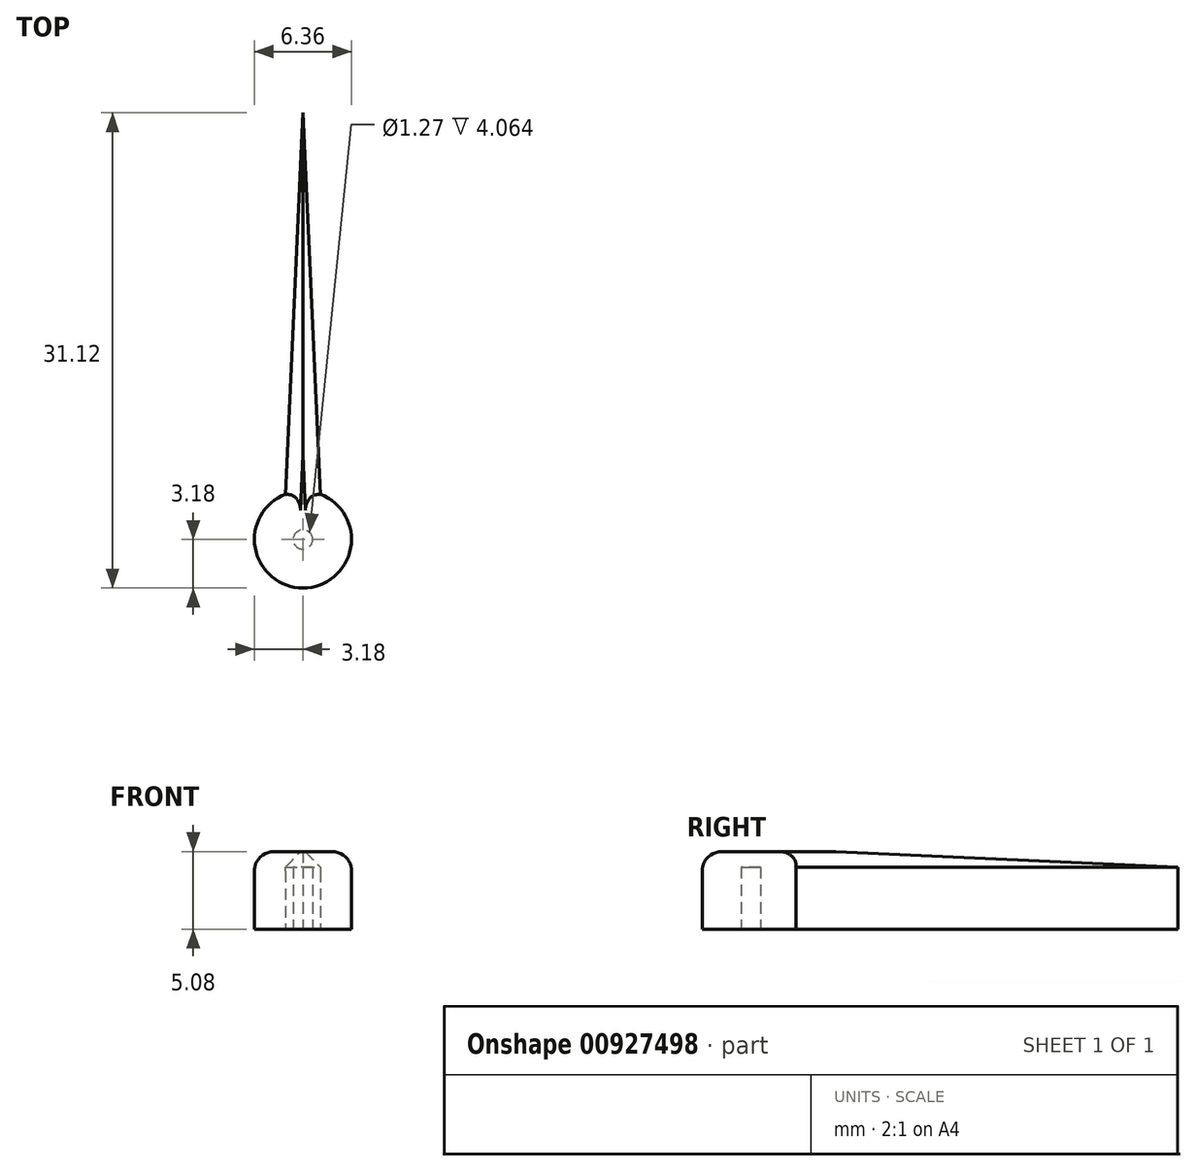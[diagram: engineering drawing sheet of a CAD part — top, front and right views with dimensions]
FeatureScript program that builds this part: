
annotation { "Feature Type Name" : "Feature", "Feature Type Description" : "" }
export const myFeature = defineFeature(function(context is Context, id is Id, definition is map)
    precondition{}
    {
        {
            var Q0;
            Q0=qCreatedBy(makeId("Top.planeOp"),FACE);
            var sketch = newSketch(context, id + "F0", { "sketchPlane" : qUnion([Q0])});
            skLineSegment(sketch, "E0", {"start": v(-1.27, 0) * mm, "end": v(0, 27.94) * mm});
            skLineSegment(sketch, "E1", {"start": v(0, 27.94) * mm, "end": v(1.27, 0) * mm});
            skLineSegment(sketch, "E2", {"start": v(0, 0) * mm, "end": v(-1.27, 0) * mm});
            skLineSegment(sketch, "E3", {"start": v(0, 0) * mm, "end": v(1.27, 0) * mm});
            skCircle(sketch, "E4", {"center": v(0, 0) * mm, "radius": 3.18 * mm});
            skSolve(sketch);
        }
        {
            var Q0;
            Q0=qSketchRegion(id+"F0",true);
            var Q1;
            {var subQ0=sQuery(id+"F0.wireOp",EDGE,"E3");var subQ1=sQuery(id+"F0.wireOp",EDGE,"E2");var subQ2=makeQuery(id+"F0.imprint","INTERSECT",VERTEX,{"derivedFrom":[subQ1,subQ0]});Q1=makeQuery(id+"F0.imprint","IMPRINT",FACE,{"disambiguationData":[TD([[makeQuery(id+"F0.imprint","IMPRINT",EDGE,{"disambiguationData":[TD([[subQ2,-1.0]])],"derivedFrom":subQ1}),-1.0]])]});}
            var Q2;
            {var subQ0=sQuery(id+"F0.wireOp",EDGE,"E3");var subQ1=sQuery(id+"F0.wireOp",EDGE,"E2");var subQ2=makeQuery(id+"F0.imprint","INTERSECT",VERTEX,{"derivedFrom":[subQ1,subQ0]});Q2=makeQuery(id+"F0.imprint","IMPRINT",FACE,{"disambiguationData":[TD([[makeQuery(id+"F0.imprint","IMPRINT",EDGE,{"disambiguationData":[TD([[subQ2,-1.0]])],"derivedFrom":subQ1}),1.0]])]});}
            extrude(context, id + "F1", {"entities" : qUnion([Q0, Q1, Q2]), "depth" : 5.08 * mm, "offsetDistance" : 25.4 * mm});
        }
        {
            var Q0;
            Q0=makeQuery(id+"F1.opExtrude","CAP_EDGE",EDGE,{"disambiguationData":[OSD([sQuery(id+"F0.wireOp",EDGE,"E0")])],"isStart":false});
            var Q1;
            Q1=makeQuery(id+"F1.opExtrude","CAP_EDGE",EDGE,{"disambiguationData":[OSD([sQuery(id+"F0.wireOp",EDGE,"E1")])],"isStart":false});
            chamfer(context, id + "F2", {"entities" : qUnion([Q0, Q1]), "width" : 1.02 * mm, "tangentPropagation" : true});
        }
        {
            var Q0;
            Q0=makeQuery(id+"F1.opExtrude","CAP_EDGE",EDGE,{"disambiguationData":[OSD([sQuery(id+"F0.wireOp",EDGE,"E4")])],"isStart":false});
            fillet(context, id + "F3", {"entities" : qUnion([Q0]), "radius" : 1.27 * mm, "tangentPropagation" : true, "allowEdgeOverflow" : false});
        }
        {
            var Q0;
            Q0=qCreatedBy(makeId("Top.planeOp"),FACE);
            var sketch = newSketch(context, id + "F4", { "sketchPlane" : qUnion([Q0])});
            skCircle(sketch, "E5", {"center": v(0, 0) * mm, "radius": 0.64 * mm});
            skSolve(sketch);
        }
        {
            var Q0;
            Q0=qSketchRegion(id+"F4",true);
            extrude(context, id + "F5", {"entities" : qUnion([Q0]), "operationType" : NewBodyOperationType.REMOVE, "depth" : 4.06 * mm, "offsetDistance" : 25.4 * mm});
        }
    });
